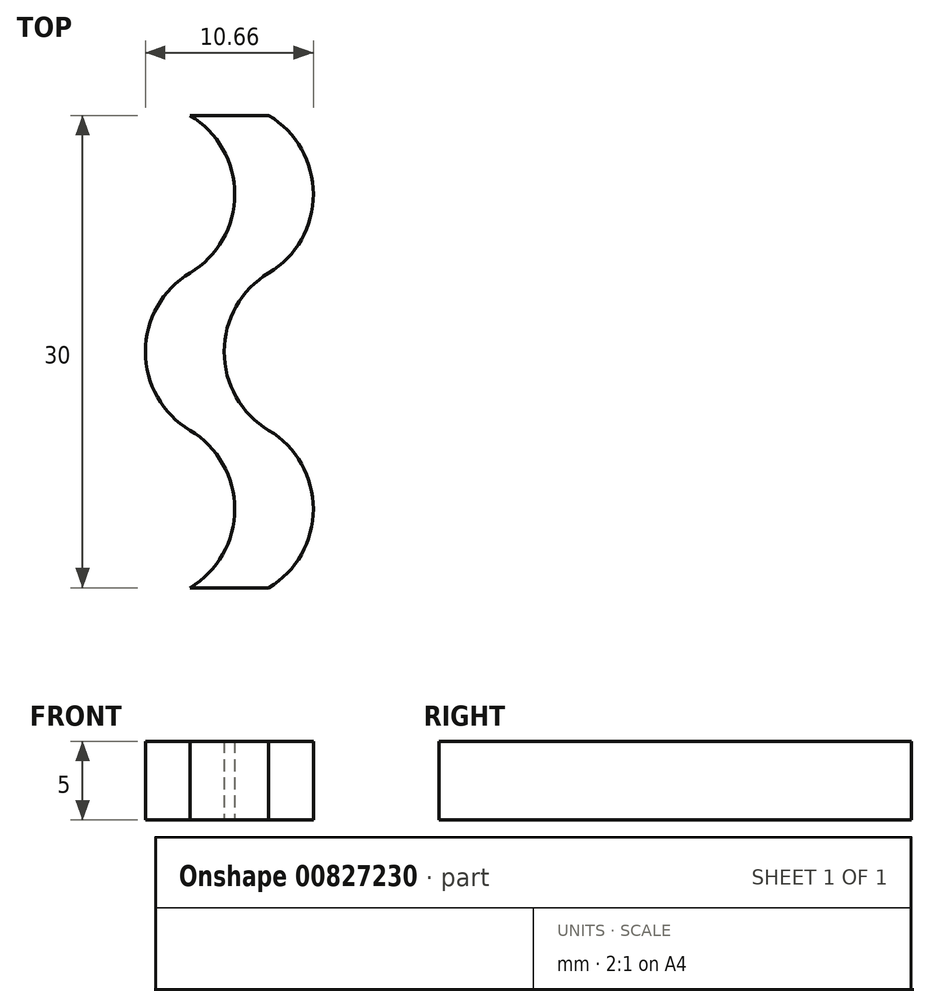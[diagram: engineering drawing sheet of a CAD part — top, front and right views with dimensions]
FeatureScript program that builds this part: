
annotation { "Feature Type Name" : "Feature", "Feature Type Description" : "" }
export const myFeature = defineFeature(function(context is Context, id is Id, definition is map)
    precondition{}
    {
        {
            var Q0;
            Q0=qCreatedBy(makeId("Top.planeOp"),FACE);
            var sketch = newSketch(context, id + "F0", { "sketchPlane" : qUnion([Q0])});
            skArc(sketch, "E0", {"start": v(0, -66.28) * mm, "mid": v(2.83, -61.28) * mm, "end": v(0, -56.28) * mm});
            skArc(sketch, "E1", {"start": v(0, -46.28) * mm, "mid": v(-2.83, -51.28) * mm, "end": v(0, -56.28) * mm});
            skArc(sketch, "E2", {"start": v(0, -46.28) * mm, "mid": v(2.83, -41.28) * mm, "end": v(0, -36.28) * mm});
            skLineSegment(sketch, "E3", {"start": v(0, -36.28) * mm, "end": v(5, -36.28) * mm});
            skArc(sketch, "E4", {"start": v(5, -66.28) * mm, "mid": v(7.83, -61.28) * mm, "end": v(5, -56.28) * mm});
            skArc(sketch, "E5", {"start": v(5, -46.28) * mm, "mid": v(2.17, -51.28) * mm, "end": v(5, -56.28) * mm});
            skLineSegment(sketch, "E6", {"start": v(0, -66.28) * mm, "end": v(5, -66.28) * mm});
            skArc(sketch, "E7", {"start": v(5, -46.28) * mm, "mid": v(7.83, -41.28) * mm, "end": v(5, -36.28) * mm});
            skSolve(sketch);
        }
        {
            var Q0;
            Q0=makeQuery(id+"F0.imprint","IMPRINT",FACE,{"disambiguationData":[TD([[makeQuery(id+"F0.imprint","IMPRINT",EDGE,{"derivedFrom":sQuery(id+"F0.wireOp",EDGE,"E0")}),-1.0]])]});
            extrude(context, id + "F1", {"entities" : qUnion([Q0]), "depth" : 5 * mm, "offsetDistance" : 25 * mm});
        }
    });
